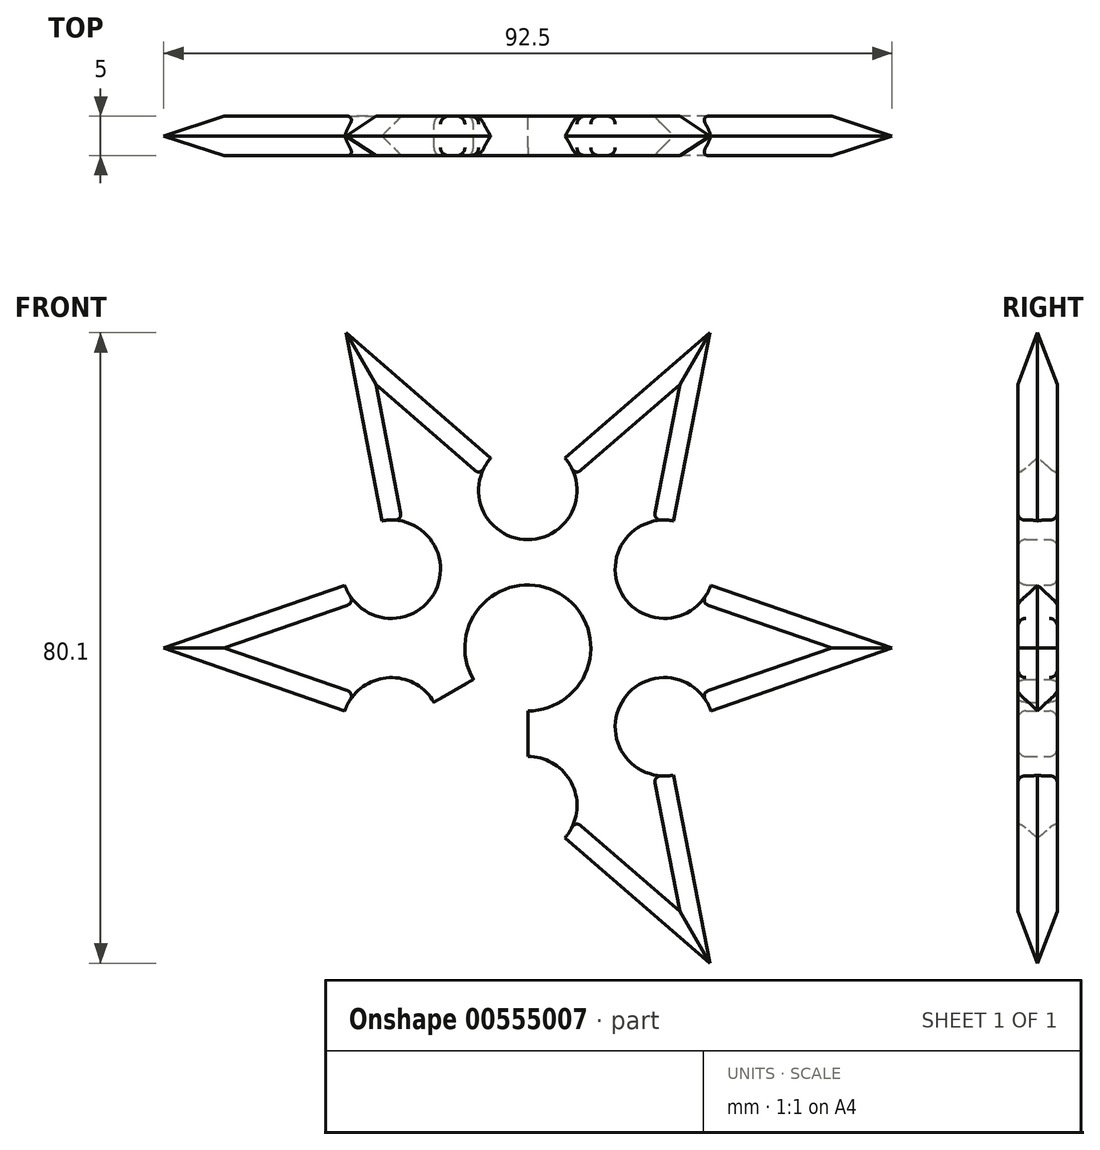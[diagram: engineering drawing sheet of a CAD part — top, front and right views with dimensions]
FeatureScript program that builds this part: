
annotation { "Feature Type Name" : "Feature", "Feature Type Description" : "" }
export const myFeature = defineFeature(function(context is Context, id is Id, definition is map)
    precondition{}
    {
        {
            var Q0;
            Q0=qCreatedBy(makeId("Front.planeOp"),FACE);
            var sketch = newSketch(context, id + "F0", { "sketchPlane" : qUnion([Q0])});
            skLineSegment(sketch, "E0", {"start": v(-11.93, -6.89) * mm, "end": v(0, 0) * mm});
            skLineSegment(sketch, "E1", {"start": v(0, 0) * mm, "end": v(-11.93, 6.89) * mm});
            skLineSegment(sketch, "E2", {"start": v(0, -13.78) * mm, "end": v(0, 0) * mm});
            skLineSegment(sketch, "E3", {"start": v(0, 0) * mm, "end": v(11.93, 6.89) * mm});
            skLineSegment(sketch, "E4", {"start": v(0, 13.78) * mm, "end": v(0, 0) * mm});
            skLineSegment(sketch, "E5", {"start": v(0, 0) * mm, "end": v(11.93, -6.89) * mm});
            skLineSegment(sketch, "E6", {"start": v(-23.12, -40.05) * mm, "end": v(-18.52, -16.15) * mm});
            skLineSegment(sketch, "E7", {"start": v(-18.52, -16.15) * mm, "end": v(-23.12, -40.05) * mm});
            skLineSegment(sketch, "E8", {"start": v(4.72, -24.12) * mm, "end": v(23.12, -40.05) * mm});
            skLineSegment(sketch, "E9", {"start": v(23.12, -40.05) * mm, "end": v(18.52, -16.15) * mm});
            skLineSegment(sketch, "E10", {"start": v(-23.12, -40.05) * mm, "end": v(-4.72, -24.12) * mm});
            skLineSegment(sketch, "E11", {"start": v(23.25, -7.97) * mm, "end": v(46.25, 0) * mm});
            skLineSegment(sketch, "E12", {"start": v(-23.25, -7.97) * mm, "end": v(-46.25, 0) * mm});
            skLineSegment(sketch, "E13.MirrorCS", {"start": v(23.25, 7.97) * mm, "end": v(46.25, 0) * mm});
            skLineSegment(sketch, "E14.MirrorCS", {"start": v(23.12, 40.05) * mm, "end": v(18.52, 16.15) * mm});
            skLineSegment(sketch, "E15.MirrorCS", {"start": v(4.72, 24.12) * mm, "end": v(23.12, 40.05) * mm});
            skLineSegment(sketch, "E16.MirrorCS", {"start": v(-23.12, 40.05) * mm, "end": v(-4.72, 24.12) * mm});
            skLineSegment(sketch, "E17.MirrorCS", {"start": v(-18.52, 16.15) * mm, "end": v(-23.12, 40.05) * mm});
            skLineSegment(sketch, "E18.MirrorCS", {"start": v(-23.25, 7.97) * mm, "end": v(-46.25, 0) * mm});
            skPoint(sketch, "E19.orphan", {"position": v(23.12, 40.05) * mm});
            skPoint(sketch, "E20.4.start.orphan", {"position": v(-23.12, 40.05) * mm});
            skArc(sketch, "E21", {"start": v(-23.25, 7.97) * mm, "mid": v(-11.93, 6.89) * mm, "end": v(-18.52, 16.15) * mm});
            skCircle(sketch, "E22", {"center": v(0, 0) * mm, "radius": 8 * mm});
            skArc(sketch, "E23", {"start": v(-18.52, -16.15) * mm, "mid": v(-11.93, -6.89) * mm, "end": v(-23.25, -7.97) * mm});
            skArc(sketch, "E24.MirrorC", {"start": v(23.25, 7.97) * mm, "mid": v(11.93, 6.89) * mm, "end": v(18.52, 16.15) * mm});
            skArc(sketch, "E25.MirrorC", {"start": v(18.52, -16.15) * mm, "mid": v(11.93, -6.89) * mm, "end": v(23.25, -7.97) * mm});
            skArc(sketch, "E26", {"start": v(-4.72, 24.12) * mm, "mid": v(0, 13.78) * mm, "end": v(4.72, 24.12) * mm});
            skArc(sketch, "E27.MirrorC", {"start": v(-4.72, -24.12) * mm, "mid": v(0, -13.78) * mm, "end": v(4.72, -24.12) * mm});
            skSolve(sketch);
        }
        {
            var Q0;
            {var subQ0=sQuery(id+"F0.wireOp",EDGE,"E12");Q0=makeQuery(id+"F0.imprint","IMPRINT",FACE,{"disambiguationData":[TD([[makeQuery(id+"F0.imprint","IMPRINT",EDGE,{"derivedFrom":subQ0}),-1.0]])]});}
            var Q1;
            {var subQ1=sQuery(id+"F0.wireOp",EDGE,"E16.MirrorCS");Q1=makeQuery(id+"F0.imprint","IMPRINT",FACE,{"disambiguationData":[TD([[makeQuery(id+"F0.imprint","IMPRINT",EDGE,{"derivedFrom":subQ1}),-1.0]])]});}
            var Q2;
            {var subQ1=sQuery(id+"F0.wireOp",EDGE,"E14.MirrorCS");Q2=makeQuery(id+"F0.imprint","IMPRINT",FACE,{"disambiguationData":[TD([[makeQuery(id+"F0.imprint","IMPRINT",EDGE,{"derivedFrom":subQ1}),-1.0]])]});}
            var Q3;
            {var subQ6=sQuery(id+"F0.wireOp",EDGE,"E11");Q3=makeQuery(id+"F0.imprint","IMPRINT",FACE,{"disambiguationData":[TD([[makeQuery(id+"F0.imprint","IMPRINT",EDGE,{"derivedFrom":subQ6}),1.0]])]});}
            var Q4;
            {var subQ0=sQuery(id+"F0.wireOp",EDGE,"E8");Q4=makeQuery(id+"F0.imprint","IMPRINT",FACE,{"disambiguationData":[TD([[makeQuery(id+"F0.imprint","IMPRINT",EDGE,{"derivedFrom":subQ0}),1.0]])]});}
            var Q5;
            {var subQ0=sQuery(id+"F0.wireOp",EDGE,"E7");Q5=makeQuery(id+"F0.imprint","IMPRINT",FACE,{"disambiguationData":[TD([[makeQuery(id+"F0.imprint","IMPRINT",EDGE,{"derivedFrom":subQ0}),1.0]])]});}
            extrude(context, id + "F1", {"entities" : qUnion([Q0, Q1, Q2, Q3, Q4, Q5]), "endBound" : BoundingType.SYMMETRIC, "depth" : 5 * mm, "offsetDistance" : 25 * mm});
        }
        {
            var Q0;
            Q0=makeQuery(id+"F1.opExtrude","CAP_EDGE",EDGE,{"disambiguationData":[OSD([sQuery(id+"F0.wireOp",EDGE,"E7")])],"isStart":false});
            var Q1;
            Q1=makeQuery(id+"F1.opExtrude","CAP_EDGE",EDGE,{"disambiguationData":[OSD([sQuery(id+"F0.wireOp",EDGE,"E10")])],"isStart":false});
            var Q2;
            Q2=makeQuery(id+"F1.opExtrude","CAP_EDGE",EDGE,{"disambiguationData":[OSD([sQuery(id+"F0.wireOp",EDGE,"E8")])],"isStart":false});
            var Q3;
            Q3=makeQuery(id+"F1.opExtrude","CAP_EDGE",EDGE,{"disambiguationData":[OSD([sQuery(id+"F0.wireOp",EDGE,"E9")])],"isStart":false});
            var Q4;
            Q4=makeQuery(id+"F1.opExtrude","CAP_EDGE",EDGE,{"disambiguationData":[OSD([sQuery(id+"F0.wireOp",EDGE,"E11")])],"isStart":false});
            var Q5;
            Q5=makeQuery(id+"F1.opExtrude","CAP_EDGE",EDGE,{"disambiguationData":[OSD([sQuery(id+"F0.wireOp",EDGE,"E13.MirrorCS")])],"isStart":false});
            var Q6;
            Q6=makeQuery(id+"F1.opExtrude","CAP_EDGE",EDGE,{"disambiguationData":[OSD([sQuery(id+"F0.wireOp",EDGE,"E14.MirrorCS")])],"isStart":false});
            var Q7;
            Q7=makeQuery(id+"F1.opExtrude","CAP_EDGE",EDGE,{"disambiguationData":[OSD([sQuery(id+"F0.wireOp",EDGE,"E15.MirrorCS")])],"isStart":false});
            var Q8;
            Q8=makeQuery(id+"F1.opExtrude","CAP_EDGE",EDGE,{"disambiguationData":[OSD([sQuery(id+"F0.wireOp",EDGE,"E16.MirrorCS")])],"isStart":false});
            var Q9;
            Q9=makeQuery(id+"F1.opExtrude","CAP_EDGE",EDGE,{"disambiguationData":[OSD([sQuery(id+"F0.wireOp",EDGE,"E17.MirrorCS")])],"isStart":false});
            var Q10;
            Q10=makeQuery(id+"F1.opExtrude","CAP_EDGE",EDGE,{"disambiguationData":[OSD([sQuery(id+"F0.wireOp",EDGE,"E18.MirrorCS")])],"isStart":false});
            var Q11;
            Q11=makeQuery(id+"F1.opExtrude","CAP_EDGE",EDGE,{"disambiguationData":[OSD([sQuery(id+"F0.wireOp",EDGE,"E12")])],"isStart":false});
            var Q12;
            Q12=makeQuery(id+"F1.opExtrude","CAP_EDGE",EDGE,{"disambiguationData":[OSD([sQuery(id+"F0.wireOp",EDGE,"E7")])],"isStart":true});
            var Q13;
            Q13=makeQuery(id+"F1.opExtrude","CAP_EDGE",EDGE,{"disambiguationData":[OSD([sQuery(id+"F0.wireOp",EDGE,"E10")])],"isStart":true});
            var Q14;
            Q14=makeQuery(id+"F1.opExtrude","CAP_EDGE",EDGE,{"disambiguationData":[OSD([sQuery(id+"F0.wireOp",EDGE,"E8")])],"isStart":true});
            var Q15;
            Q15=makeQuery(id+"F1.opExtrude","CAP_EDGE",EDGE,{"disambiguationData":[OSD([sQuery(id+"F0.wireOp",EDGE,"E9")])],"isStart":true});
            var Q16;
            Q16=makeQuery(id+"F1.opExtrude","CAP_EDGE",EDGE,{"disambiguationData":[OSD([sQuery(id+"F0.wireOp",EDGE,"E12")])],"isStart":true});
            var Q17;
            Q17=makeQuery(id+"F1.opExtrude","CAP_EDGE",EDGE,{"disambiguationData":[OSD([sQuery(id+"F0.wireOp",EDGE,"E18.MirrorCS")])],"isStart":true});
            var Q18;
            Q18=makeQuery(id+"F1.opExtrude","CAP_EDGE",EDGE,{"disambiguationData":[OSD([sQuery(id+"F0.wireOp",EDGE,"E17.MirrorCS")])],"isStart":true});
            var Q19;
            Q19=makeQuery(id+"F1.opExtrude","CAP_EDGE",EDGE,{"disambiguationData":[OSD([sQuery(id+"F0.wireOp",EDGE,"E15.MirrorCS")])],"isStart":true});
            var Q20;
            Q20=makeQuery(id+"F1.opExtrude","CAP_EDGE",EDGE,{"disambiguationData":[OSD([sQuery(id+"F0.wireOp",EDGE,"E14.MirrorCS")])],"isStart":true});
            var Q21;
            Q21=makeQuery(id+"F1.opExtrude","CAP_EDGE",EDGE,{"disambiguationData":[OSD([sQuery(id+"F0.wireOp",EDGE,"E16.MirrorCS")])],"isStart":true});
            var Q22;
            Q22=makeQuery(id+"F1.opExtrude","CAP_EDGE",EDGE,{"disambiguationData":[OSD([sQuery(id+"F0.wireOp",EDGE,"E13.MirrorCS")])],"isStart":true});
            var Q23;
            Q23=makeQuery(id+"F1.opExtrude","CAP_EDGE",EDGE,{"disambiguationData":[OSD([sQuery(id+"F0.wireOp",EDGE,"E11")])],"isStart":true});
            chamfer(context, id + "F2", {"entities" : qUnion([Q0, Q1, Q2, Q3, Q4, Q5, Q6, Q7, Q8, Q9, Q10, Q11, Q12, Q13, Q14, Q15, Q16, Q17, Q18, Q19, Q20, Q21, Q22, Q23]), "width" : 2.5 * mm, "tangentPropagation" : true});
        }
        {
            var Q0;
            Q0=makeQuery(id+"F1.opExtrude","CAP_EDGE",EDGE,{"disambiguationData":[OSD([sQuery(id+"F0.wireOp",EDGE,"E22")])],"isStart":true});
            var Q1;
            Q1=makeQuery(id+"F1.opExtrude","CAP_EDGE",EDGE,{"disambiguationData":[OSD([sQuery(id+"F0.wireOp",EDGE,"E21")])],"isStart":true});
            var Q2;
            Q2=makeQuery(id+"F1.opExtrude","CAP_EDGE",EDGE,{"disambiguationData":[OSD([sQuery(id+"F0.wireOp",EDGE,"E26")])],"isStart":true});
            var Q3;
            Q3=makeQuery(id+"F1.opExtrude","CAP_EDGE",EDGE,{"disambiguationData":[OSD([sQuery(id+"F0.wireOp",EDGE,"E24.MirrorC")])],"isStart":true});
            var Q4;
            Q4=makeQuery(id+"F1.opExtrude","CAP_EDGE",EDGE,{"disambiguationData":[OSD([sQuery(id+"F0.wireOp",EDGE,"E27.MirrorC")])],"isStart":true});
            var Q5;
            Q5=makeQuery(id+"F1.opExtrude","CAP_EDGE",EDGE,{"disambiguationData":[OSD([sQuery(id+"F0.wireOp",EDGE,"E23")])],"isStart":true});
            var Q6;
            Q6=makeQuery(id+"F1.opExtrude","CAP_EDGE",EDGE,{"disambiguationData":[OSD([sQuery(id+"F0.wireOp",EDGE,"E25.MirrorC")])],"isStart":true});
            var Q7;
            Q7=makeQuery(id+"F1.opExtrude","CAP_EDGE",EDGE,{"disambiguationData":[OSD([sQuery(id+"F0.wireOp",EDGE,"E26")])],"isStart":false});
            var Q8;
            Q8=makeQuery(id+"F1.opExtrude","CAP_EDGE",EDGE,{"disambiguationData":[OSD([sQuery(id+"F0.wireOp",EDGE,"E21")])],"isStart":false});
            var Q9;
            Q9=makeQuery(id+"F1.opExtrude","CAP_EDGE",EDGE,{"disambiguationData":[OSD([sQuery(id+"F0.wireOp",EDGE,"E23")])],"isStart":false});
            var Q10;
            Q10=makeQuery(id+"F1.opExtrude","CAP_EDGE",EDGE,{"disambiguationData":[OSD([sQuery(id+"F0.wireOp",EDGE,"E22")])],"isStart":false});
            var Q11;
            Q11=makeQuery(id+"F1.opExtrude","CAP_EDGE",EDGE,{"disambiguationData":[OSD([sQuery(id+"F0.wireOp",EDGE,"E24.MirrorC")])],"isStart":false});
            var Q12;
            Q12=makeQuery(id+"F1.opExtrude","CAP_EDGE",EDGE,{"disambiguationData":[OSD([sQuery(id+"F0.wireOp",EDGE,"E25.MirrorC")])],"isStart":false});
            var Q13;
            Q13=makeQuery(id+"F1.opExtrude","CAP_EDGE",EDGE,{"disambiguationData":[OSD([sQuery(id+"F0.wireOp",EDGE,"E27.MirrorC")])],"isStart":false});
            fillet(context, id + "F3", {"entities" : qUnion([Q0, Q1, Q2, Q3, Q4, Q5, Q6, Q7, Q8, Q9, Q10, Q11, Q12, Q13]), "radius" : 1 * mm, "tangentPropagation" : true, "allowEdgeOverflow" : false});
        }
    });
